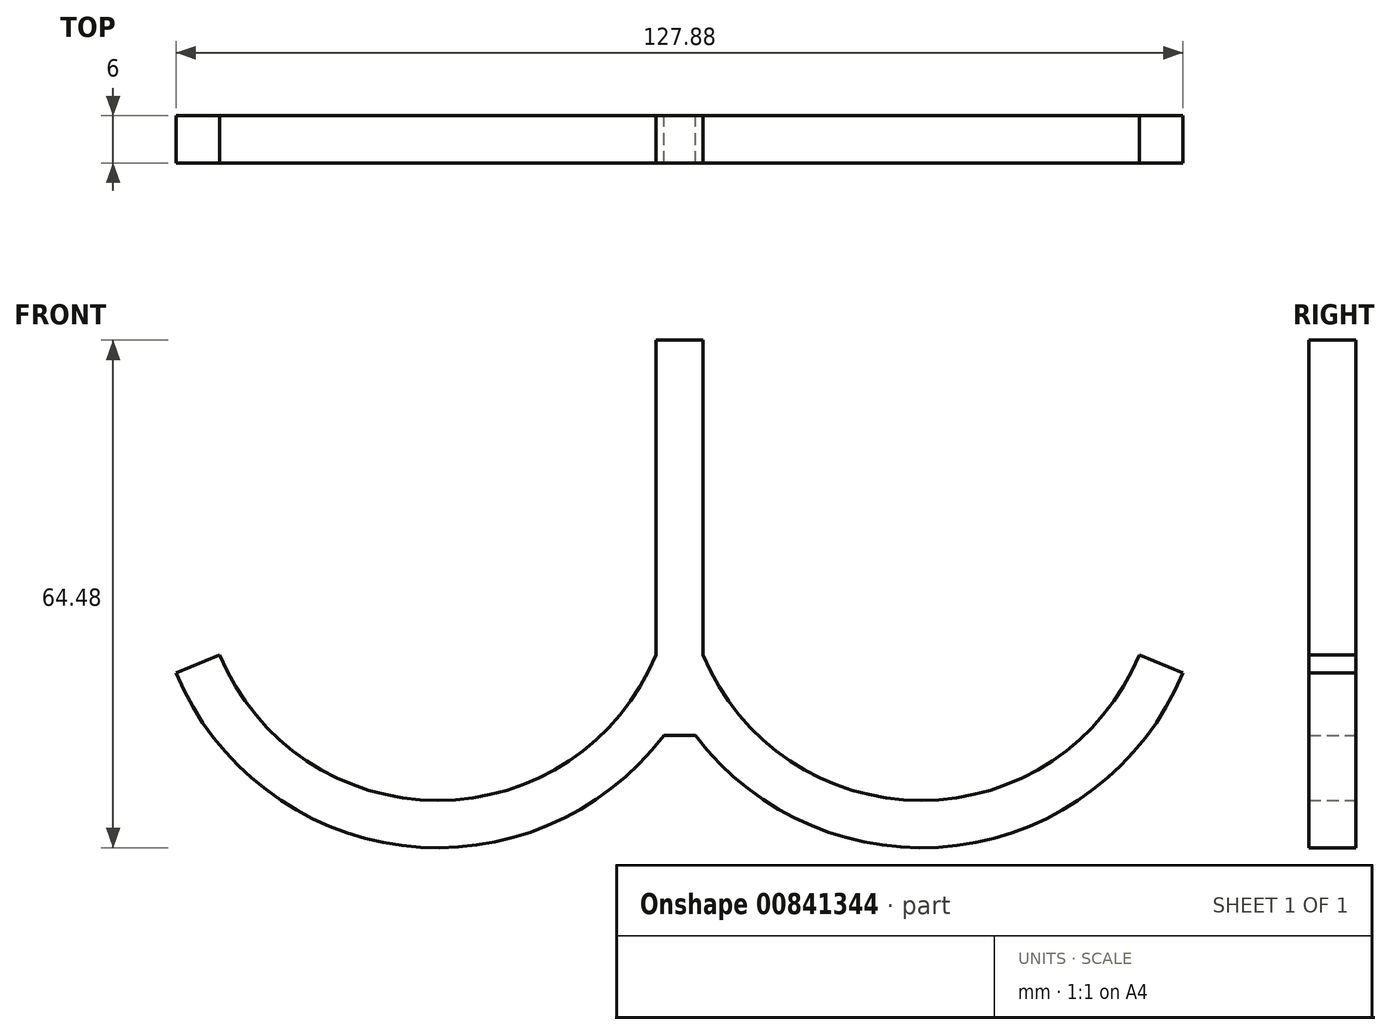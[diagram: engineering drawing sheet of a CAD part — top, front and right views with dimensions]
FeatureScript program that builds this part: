
annotation { "Feature Type Name" : "Feature", "Feature Type Description" : "" }
export const myFeature = defineFeature(function(context is Context, id is Id, definition is map)
    precondition{}
    {
        {
            var Q0;
            Q0=qCreatedBy(makeId("Front.planeOp"),FACE);
            var sketch = newSketch(context, id + "F0", { "sketchPlane" : qUnion([Q0])});
            skLineSegment(sketch, "E0", {"start": v(-3, 34.67) * mm, "end": v(-3, -5.33) * mm});
            skArc(sketch, "E1", {"start": v(-58.4, -5.33) * mm, "mid": v(-30.7, -23.81) * mm, "end": v(-3, -5.33) * mm});
            skLineSegment(sketch, "E2.MirrorCS", {"start": v(3, 34.67) * mm, "end": v(3, -5.33) * mm});
            skArc(sketch, "E3.MirrorCS", {"start": v(58.4, -5.33) * mm, "mid": v(30.7, -23.81) * mm, "end": v(3, -5.33) * mm});
            skLineSegment(sketch, "E4", {"start": v(-3, 34.67) * mm, "end": v(3, 34.67) * mm});
            skArc(sketch, "E5.0", {"start": v(-63.94, -7.64) * mm, "mid": v(-35.26, -29.52) * mm, "end": v(-2, -15.55) * mm});
            skArc(sketch, "E6.MirrorCS", {"start": v(63.94, -7.64) * mm, "mid": v(35.26, -29.52) * mm, "end": v(2, -15.55) * mm});
            skLineSegment(sketch, "E7", {"start": v(-58.4, -5.33) * mm, "end": v(-63.94, -7.64) * mm});
            skLineSegment(sketch, "E8", {"start": v(58.4, -5.33) * mm, "end": v(63.94, -7.64) * mm});
            skLineSegment(sketch, "E9", {"start": v(2, -15.55) * mm, "end": v(-2, -15.55) * mm});
            skLineSegment(sketch, "E10", {"start": v(-3, -5.33) * mm, "end": v(3, -5.33) * mm, "construction": true});
            skSolve(sketch);
        }
        {
            var Q0;
            Q0 = qSketchRegion(id + "F0", true);
            extrude(context, id + "F1", {"entities" : qUnion([Q0]), "endBound" : BoundingType.SYMMETRIC, "depth" : 6 * mm, "offsetDistance" : 25 * mm});
        }
    });
